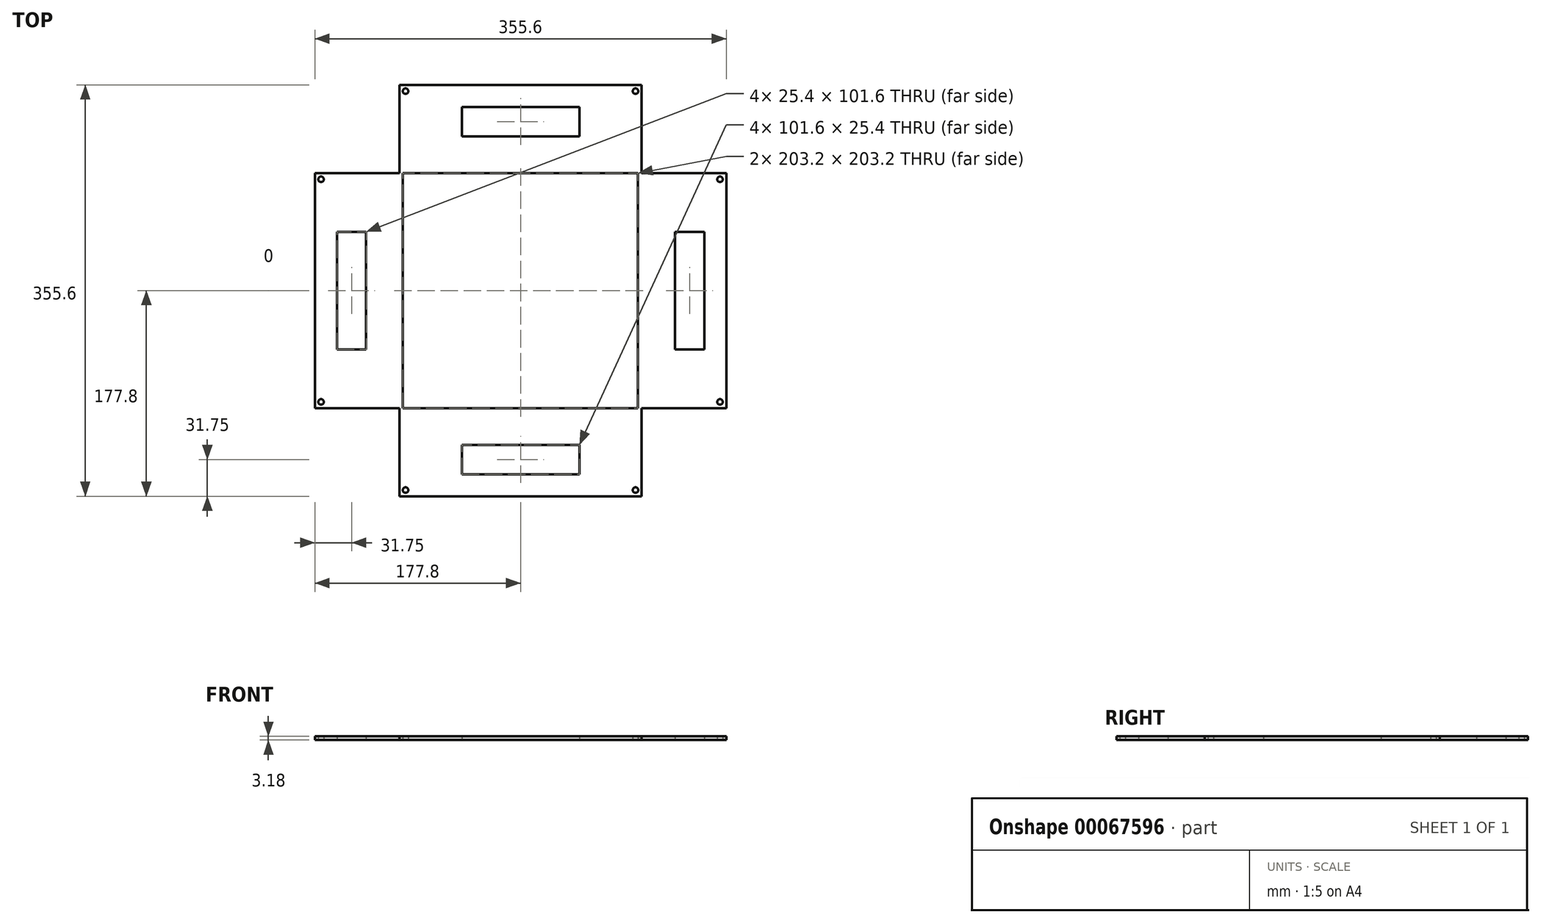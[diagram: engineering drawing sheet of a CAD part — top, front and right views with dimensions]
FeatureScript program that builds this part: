
annotation { "Feature Type Name" : "Feature", "Feature Type Description" : "" }
export const myFeature = defineFeature(function(context is Context, id is Id, definition is map)
    precondition{}
    {
        {
            var Q0;
            Q0=qCreatedBy(makeId("Top.planeOp"),FACE);
            var sketch = newSketch(context, id + "F0", { "sketchPlane" : qUnion([Q0])});
            skLineSegment(sketch, "E0", {"start": v(0, 0) * mm, "end": v(0, 203.2) * mm});
            skLineSegment(sketch, "E1", {"start": v(203.2, 0) * mm, "end": v(0, 0) * mm});
            skLineSegment(sketch, "E2", {"start": v(203.2, 0) * mm, "end": v(206.38, 0) * mm});
            skLineSegment(sketch, "E3", {"start": v(206.38, 0) * mm, "end": v(206.38, -76.2) * mm});
            skLineSegment(sketch, "E4", {"start": v(206.38, -76.2) * mm, "end": v(-3.18, -76.2) * mm});
            skLineSegment(sketch, "E5", {"start": v(-3.18, -76.2) * mm, "end": v(-3.18, 0) * mm});
            skLineSegment(sketch, "E6", {"start": v(-3.18, 0) * mm, "end": v(0, 0) * mm});
            skLineSegment(sketch, "E7.rect.bottom", {"start": v(152.4, -31.75) * mm, "end": v(50.8, -31.75) * mm});
            skLineSegment(sketch, "E7.rect.top", {"start": v(152.4, -57.15) * mm, "end": v(50.8, -57.15) * mm});
            skLineSegment(sketch, "E7.rect.left", {"start": v(152.4, -31.75) * mm, "end": v(152.4, -57.15) * mm});
            skLineSegment(sketch, "E7.rect.right", {"start": v(50.8, -31.75) * mm, "end": v(50.8, -57.15) * mm});
            skPoint(sketch, "E7.rect.middle", {"position": v(101.6, -44.45) * mm});
            skLineSegment(sketch, "E8", {"start": v(0, 203.2) * mm, "end": v(-76.2, 203.2) * mm});
            skLineSegment(sketch, "E9", {"start": v(-76.2, 203.2) * mm, "end": v(-76.2, 0) * mm});
            skLineSegment(sketch, "E10", {"start": v(-76.2, 0) * mm, "end": v(0, 0) * mm});
            skLineSegment(sketch, "E11.rect.bottom", {"start": v(-57.15, 50.8) * mm, "end": v(-31.75, 50.8) * mm});
            skLineSegment(sketch, "E11.rect.top", {"start": v(-57.15, 152.4) * mm, "end": v(-31.75, 152.4) * mm});
            skLineSegment(sketch, "E11.rect.left", {"start": v(-57.15, 50.8) * mm, "end": v(-57.15, 152.4) * mm});
            skLineSegment(sketch, "E11.rect.right", {"start": v(-31.75, 50.8) * mm, "end": v(-31.75, 152.4) * mm});
            skPoint(sketch, "E11.rect.middle", {"position": v(-44.45, 101.6) * mm});
            skLineSegment(sketch, "E12", {"start": v(-3.18, -76.2) * mm, "end": v(2.21, -70.81) * mm});
            skCircle(sketch, "E13", {"center": v(2.21, -70.81) * mm, "radius": 2.38 * mm});
            skLineSegment(sketch, "E14", {"start": v(-76.2, 0) * mm, "end": v(-70.81, 5.39) * mm});
            skCircle(sketch, "E15", {"center": v(-70.81, 5.39) * mm, "radius": 2.38 * mm});
            skCircle(sketch, "E16.MirrorC", {"center": v(-70.81, 197.81) * mm, "radius": 2.38 * mm});
            skLineSegment(sketch, "E17", {"start": v(206.38, -76.2) * mm, "end": v(200.99, -70.81) * mm});
            skLineSegment(sketch, "E18", {"start": v(-76.2, 203.2) * mm, "end": v(-70.81, 197.81) * mm});
            skCircle(sketch, "E19", {"center": v(200.99, -70.81) * mm, "radius": 2.38 * mm});
            skPoint(sketch, "E20.endSnap0", {"position": v(0, 101.6) * mm});
            skLineSegment(sketch, "E21.MirrorCS", {"start": v(203.2, 0) * mm, "end": v(203.2, 203.2) * mm});
            skLineSegment(sketch, "E22.MirrorCS", {"start": v(203.2, 203.2) * mm, "end": v(279.4, 203.2) * mm});
            skLineSegment(sketch, "E23.MirrorCS", {"start": v(279.4, 203.2) * mm, "end": v(279.4, 0) * mm});
            skLineSegment(sketch, "E24.MirrorCS", {"start": v(279.4, 0) * mm, "end": v(203.2, 0) * mm});
            skLineSegment(sketch, "E25.MirrorCS", {"start": v(234.95, 50.8) * mm, "end": v(234.95, 152.4) * mm});
            skLineSegment(sketch, "E26.MirrorCS", {"start": v(260.35, 152.4) * mm, "end": v(234.95, 152.4) * mm});
            skLineSegment(sketch, "E27.MirrorCS", {"start": v(260.35, 50.8) * mm, "end": v(260.35, 152.4) * mm});
            skLineSegment(sketch, "E28.MirrorCS", {"start": v(260.35, 50.8) * mm, "end": v(234.95, 50.8) * mm});
            skLineSegment(sketch, "E29.MirrorCS", {"start": v(206.38, 279.4) * mm, "end": v(-3.18, 279.4) * mm});
            skLineSegment(sketch, "E30.MirrorCS", {"start": v(152.4, 260.35) * mm, "end": v(50.8, 260.35) * mm});
            skLineSegment(sketch, "E31.MirrorCS", {"start": v(50.8, 234.95) * mm, "end": v(50.8, 260.35) * mm});
            skLineSegment(sketch, "E32.MirrorCS", {"start": v(152.4, 234.95) * mm, "end": v(50.8, 234.95) * mm});
            skLineSegment(sketch, "E33.MirrorCS", {"start": v(152.4, 234.95) * mm, "end": v(152.4, 260.35) * mm});
            skLineSegment(sketch, "E34.MirrorCS", {"start": v(206.38, 203.2) * mm, "end": v(206.38, 279.4) * mm});
            skLineSegment(sketch, "E35.MirrorCS", {"start": v(-3.18, 279.4) * mm, "end": v(-3.18, 203.2) * mm});
            skLineSegment(sketch, "E36", {"start": v(203.2, 203.2) * mm, "end": v(0, 203.2) * mm});
            skLineSegment(sketch, "E37", {"start": v(101.6, 203.2) * mm, "end": v(101.6, 0) * mm});
            skLineSegment(sketch, "E38", {"start": v(203.2, 101.6) * mm, "end": v(0, 101.6) * mm});
            skCircle(sketch, "E39.MirrorC", {"center": v(2.21, 274.01) * mm, "radius": 2.38 * mm});
            skCircle(sketch, "E40.MirrorC", {"center": v(200.99, 274.01) * mm, "radius": 2.38 * mm});
            skCircle(sketch, "E41.MirrorC", {"center": v(274.01, 197.81) * mm, "radius": 2.38 * mm});
            skCircle(sketch, "E42.MirrorC", {"center": v(274.01, 5.39) * mm, "radius": 2.38 * mm});
            skSolve(sketch);
        }
        {
            var Q0;
            Q0 = qSketchRegion(id + "F0", true);
            extrude(context, id + "F1", {"entities" : qUnion([Q0]), "depth" : 3.17 * mm});
        }
    });
